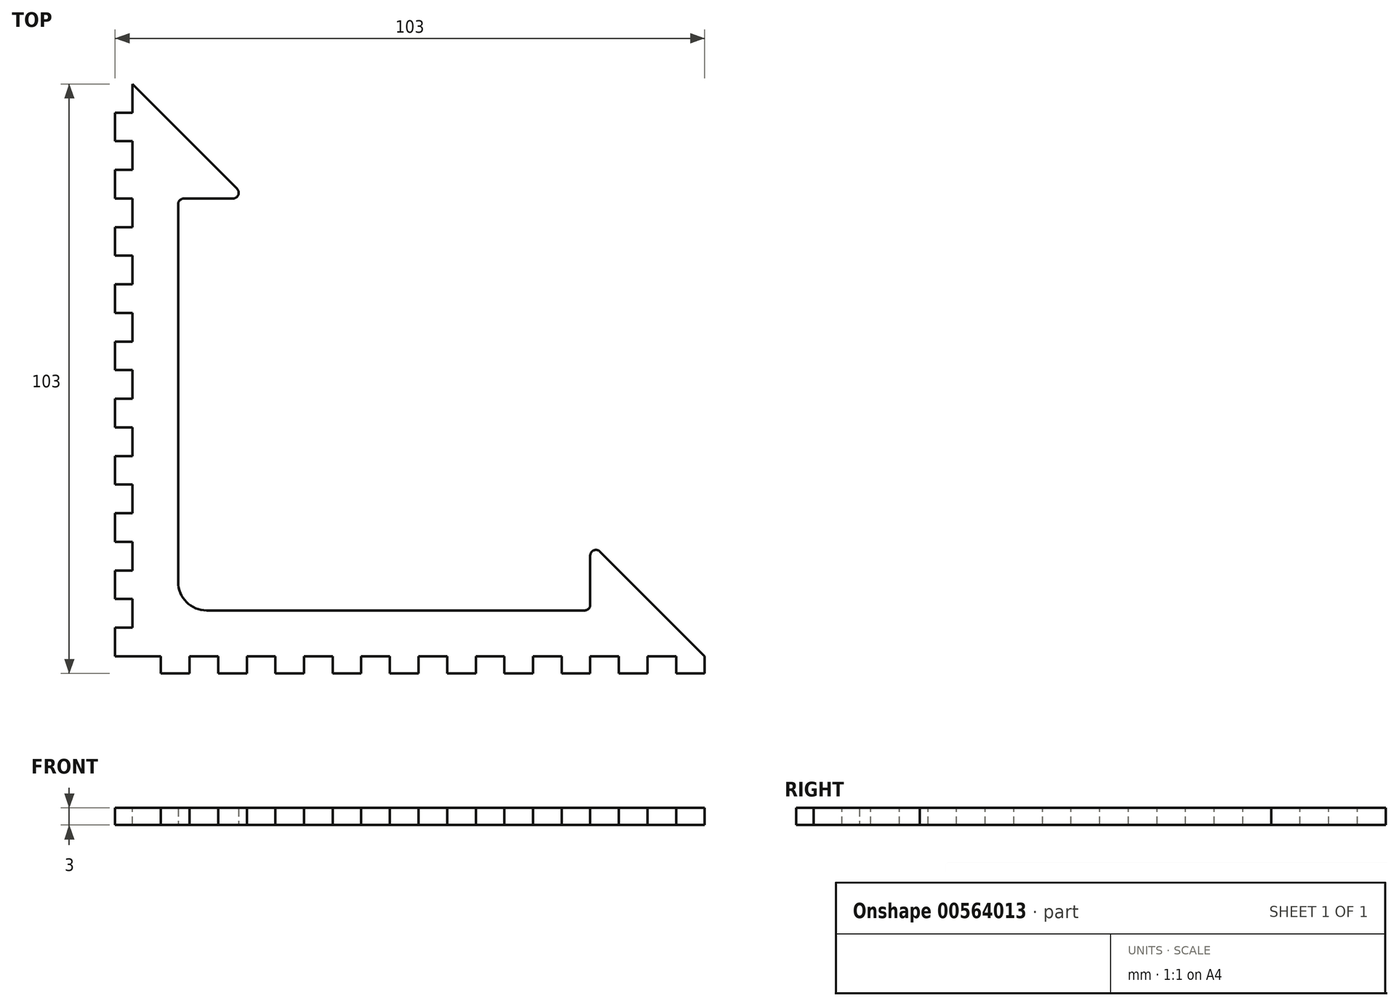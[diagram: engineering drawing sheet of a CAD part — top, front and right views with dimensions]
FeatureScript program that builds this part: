
annotation { "Feature Type Name" : "Feature", "Feature Type Description" : "" }
export const myFeature = defineFeature(function(context is Context, id is Id, definition is map)
    precondition{}
    {
        {
            var Q0;
            Q0=qCreatedBy(makeId("Top.planeOp"),FACE);
            var sketch = newSketch(context, id + "F0", { "sketchPlane" : qUnion([Q0])});
            skLineSegment(sketch, "E0", {"start": v(0, 100) * mm, "end": v(0, 0) * mm});
            skLineSegment(sketch, "E1", {"start": v(0, 0) * mm, "end": v(100, 0) * mm});
            skLineSegment(sketch, "E2", {"start": v(100, 0) * mm, "end": v(80, 20) * mm});
            skLineSegment(sketch, "E3", {"start": v(80, 20) * mm, "end": v(80, 8) * mm});
            skLineSegment(sketch, "E4", {"start": v(80, 8) * mm, "end": v(8, 8) * mm});
            skLineSegment(sketch, "E5", {"start": v(8, 8) * mm, "end": v(8, 80) * mm});
            skLineSegment(sketch, "E6", {"start": v(8, 80) * mm, "end": v(20, 80) * mm});
            skLineSegment(sketch, "E7", {"start": v(20, 80) * mm, "end": v(0, 100) * mm});
            skSolve(sketch);
        }
        {
            var Q0;
            Q0=makeQuery(id+"F0.imprint","IMPRINT",FACE,{"disambiguationData":[TD([[makeQuery(id+"F0.imprint","IMPRINT",EDGE,{"derivedFrom":sQuery(id+"F0.wireOp",EDGE,"E0")}),1.0]])]});
            extrude(context, id + "F1", {"entities" : qUnion([Q0]), "depth" : 3 * mm, "offsetDistance" : 25 * mm});
        }
        {
            var Q0;
            Q0=makeQuery(id+"F1.opExtrude","CAP_FACE",FACE,{"disambiguationData":[OSD([sQuery(id+"F0.wireOp",EDGE,"E0"),sQuery(id+"F0.wireOp",EDGE,"E1"),sQuery(id+"F0.wireOp",EDGE,"E2"),sQuery(id+"F0.wireOp",EDGE,"E3"),sQuery(id+"F0.wireOp",EDGE,"E4"),sQuery(id+"F0.wireOp",EDGE,"E5"),sQuery(id+"F0.wireOp",EDGE,"E6"),sQuery(id+"F0.wireOp",EDGE,"E7")])],"isStart":false});
            var sketch = newSketch(context, id + "F2", { "sketchPlane" : qUnion([Q0])});
            skLineSegment(sketch, "E8.bottom", {"start": v(5, 0) * mm, "end": v(10, 0) * mm});
            skLineSegment(sketch, "E8.top", {"start": v(5, -3) * mm, "end": v(10, -3) * mm});
            skLineSegment(sketch, "E8.left", {"start": v(5, 0) * mm, "end": v(5, -3) * mm});
            skLineSegment(sketch, "E8.right", {"start": v(10, 0) * mm, "end": v(10, -3) * mm});
            skLineSegment(sketch, "E9.1.0.0", {"start": v(15, 0) * mm, "end": v(20, 0) * mm});
            skLineSegment(sketch, "E9.1.0.1", {"start": v(15, 0) * mm, "end": v(15, -3) * mm});
            skLineSegment(sketch, "E9.1.0.2", {"start": v(15, -3) * mm, "end": v(20, -3) * mm});
            skLineSegment(sketch, "E9.1.0.3", {"start": v(20, 0) * mm, "end": v(20, -3) * mm});
            skLineSegment(sketch, "E9.2.0.0", {"start": v(25, 0) * mm, "end": v(30, 0) * mm});
            skLineSegment(sketch, "E9.2.0.1", {"start": v(25, 0) * mm, "end": v(25, -3) * mm});
            skLineSegment(sketch, "E9.2.0.2", {"start": v(25, -3) * mm, "end": v(30, -3) * mm});
            skLineSegment(sketch, "E9.2.0.3", {"start": v(30, 0) * mm, "end": v(30, -3) * mm});
            skLineSegment(sketch, "E9.3.0.0", {"start": v(35, 0) * mm, "end": v(40, 0) * mm});
            skLineSegment(sketch, "E9.3.0.1", {"start": v(35, 0) * mm, "end": v(35, -3) * mm});
            skLineSegment(sketch, "E9.3.0.2", {"start": v(35, -3) * mm, "end": v(40, -3) * mm});
            skLineSegment(sketch, "E9.3.0.3", {"start": v(40, 0) * mm, "end": v(40, -3) * mm});
            skLineSegment(sketch, "E9.4.0.0", {"start": v(45, 0) * mm, "end": v(50, 0) * mm});
            skLineSegment(sketch, "E9.4.0.1", {"start": v(45, 0) * mm, "end": v(45, -3) * mm});
            skLineSegment(sketch, "E9.4.0.2", {"start": v(45, -3) * mm, "end": v(50, -3) * mm});
            skLineSegment(sketch, "E9.4.0.3", {"start": v(50, 0) * mm, "end": v(50, -3) * mm});
            skLineSegment(sketch, "E9.direction1", {"start": v(5, 0) * mm, "end": v(15, 0) * mm, "construction": true});
            skLineSegment(sketch, "E10.0.5.0", {"start": v(55, 0) * mm, "end": v(60, 0) * mm});
            skLineSegment(sketch, "E10.3.5.0", {"start": v(55, 0) * mm, "end": v(55, -3) * mm});
            skLineSegment(sketch, "E10.6.5.0", {"start": v(55, -3) * mm, "end": v(60, -3) * mm});
            skLineSegment(sketch, "E10.9.5.0", {"start": v(60, 0) * mm, "end": v(60, -3) * mm});
            skLineSegment(sketch, "E10.0.6.0", {"start": v(65, 0) * mm, "end": v(70, 0) * mm});
            skLineSegment(sketch, "E10.3.6.0", {"start": v(65, 0) * mm, "end": v(65, -3) * mm});
            skLineSegment(sketch, "E10.6.6.0", {"start": v(65, -3) * mm, "end": v(70, -3) * mm});
            skLineSegment(sketch, "E10.9.6.0", {"start": v(70, 0) * mm, "end": v(70, -3) * mm});
            skLineSegment(sketch, "E10.0.7.0", {"start": v(75, 0) * mm, "end": v(80, 0) * mm});
            skLineSegment(sketch, "E10.3.7.0", {"start": v(75, 0) * mm, "end": v(75, -3) * mm});
            skLineSegment(sketch, "E10.6.7.0", {"start": v(75, -3) * mm, "end": v(80, -3) * mm});
            skLineSegment(sketch, "E10.9.7.0", {"start": v(80, 0) * mm, "end": v(80, -3) * mm});
            skLineSegment(sketch, "E10.0.8.0", {"start": v(85, 0) * mm, "end": v(90, 0) * mm});
            skLineSegment(sketch, "E10.3.8.0", {"start": v(85, 0) * mm, "end": v(85, -3) * mm});
            skLineSegment(sketch, "E10.6.8.0", {"start": v(85, -3) * mm, "end": v(90, -3) * mm});
            skLineSegment(sketch, "E10.9.8.0", {"start": v(90, 0) * mm, "end": v(90, -3) * mm});
            skLineSegment(sketch, "E10.0.9.0", {"start": v(95, 0) * mm, "end": v(100, 0) * mm});
            skLineSegment(sketch, "E10.3.9.0", {"start": v(95, 0) * mm, "end": v(95, -3) * mm});
            skLineSegment(sketch, "E10.6.9.0", {"start": v(95, -3) * mm, "end": v(100, -3) * mm});
            skLineSegment(sketch, "E10.9.9.0", {"start": v(100, 0) * mm, "end": v(100, -3) * mm});
            skSolve(sketch);
        }
        {
            var Q0;
            {var subQ2=sQuery(id+"F2.wireOp",EDGE,"E8.bottom");Q0=makeQuery(id+"F2.imprint","IMPRINT",FACE,{"disambiguationData":[TD([[makeQuery(id+"F2.imprint","IMPRINT",EDGE,{"derivedFrom":subQ2}),1.0]])]});}
            var sketch = newSketch(context, id + "F3", { "sketchPlane" : qUnion([Q0])});
            skLineSegment(sketch, "E11.bottom", {"start": v(0, 0) * mm, "end": v(-3, 0) * mm});
            skLineSegment(sketch, "E11.top", {"start": v(0, 5) * mm, "end": v(-3, 5) * mm});
            skLineSegment(sketch, "E11.left", {"start": v(0, 0) * mm, "end": v(0, 5) * mm});
            skLineSegment(sketch, "E11.right", {"start": v(-3, 0) * mm, "end": v(-3, 5) * mm});
            skLineSegment(sketch, "E12.0.1.0", {"start": v(0, 15) * mm, "end": v(-3, 15) * mm});
            skLineSegment(sketch, "E12.0.1.1", {"start": v(-3, 10) * mm, "end": v(-3, 15) * mm});
            skLineSegment(sketch, "E12.0.1.2", {"start": v(0, 10) * mm, "end": v(0, 15) * mm});
            skLineSegment(sketch, "E12.0.1.3", {"start": v(0, 10) * mm, "end": v(-3, 10) * mm});
            skLineSegment(sketch, "E12.0.2.0", {"start": v(0, 25) * mm, "end": v(-3, 25) * mm});
            skLineSegment(sketch, "E12.0.2.1", {"start": v(-3, 20) * mm, "end": v(-3, 25) * mm});
            skLineSegment(sketch, "E12.0.2.2", {"start": v(0, 20) * mm, "end": v(0, 25) * mm});
            skLineSegment(sketch, "E12.0.2.3", {"start": v(0, 20) * mm, "end": v(-3, 20) * mm});
            skLineSegment(sketch, "E12.0.3.0", {"start": v(0, 35) * mm, "end": v(-3, 35) * mm});
            skLineSegment(sketch, "E12.0.3.1", {"start": v(-3, 30) * mm, "end": v(-3, 35) * mm});
            skLineSegment(sketch, "E12.0.3.2", {"start": v(0, 30) * mm, "end": v(0, 35) * mm});
            skLineSegment(sketch, "E12.0.3.3", {"start": v(0, 30) * mm, "end": v(-3, 30) * mm});
            skLineSegment(sketch, "E12.0.4.0", {"start": v(0, 45) * mm, "end": v(-3, 45) * mm});
            skLineSegment(sketch, "E12.0.4.1", {"start": v(-3, 40) * mm, "end": v(-3, 45) * mm});
            skLineSegment(sketch, "E12.0.4.2", {"start": v(0, 40) * mm, "end": v(0, 45) * mm});
            skLineSegment(sketch, "E12.0.4.3", {"start": v(0, 40) * mm, "end": v(-3, 40) * mm});
            skLineSegment(sketch, "E12.direction1", {"start": v(-3, 5) * mm, "end": v(13.8, 5) * mm, "construction": true});
            skLineSegment(sketch, "E12.direction2", {"start": v(-3, 5) * mm, "end": v(-3, 15) * mm, "construction": true});
            skLineSegment(sketch, "E13.0.0.5", {"start": v(0, 55) * mm, "end": v(-3, 55) * mm});
            skLineSegment(sketch, "E13.3.0.5", {"start": v(-3, 50) * mm, "end": v(-3, 55) * mm});
            skLineSegment(sketch, "E13.6.0.5", {"start": v(0, 50) * mm, "end": v(0, 55) * mm});
            skLineSegment(sketch, "E13.9.0.5", {"start": v(0, 50) * mm, "end": v(-3, 50) * mm});
            skLineSegment(sketch, "E13.0.0.6", {"start": v(0, 65) * mm, "end": v(-3, 65) * mm});
            skLineSegment(sketch, "E13.3.0.6", {"start": v(-3, 60) * mm, "end": v(-3, 65) * mm});
            skLineSegment(sketch, "E13.6.0.6", {"start": v(0, 60) * mm, "end": v(0, 65) * mm});
            skLineSegment(sketch, "E13.9.0.6", {"start": v(0, 60) * mm, "end": v(-3, 60) * mm});
            skLineSegment(sketch, "E13.0.0.7", {"start": v(0, 75) * mm, "end": v(-3, 75) * mm});
            skLineSegment(sketch, "E13.3.0.7", {"start": v(-3, 70) * mm, "end": v(-3, 75) * mm});
            skLineSegment(sketch, "E13.6.0.7", {"start": v(0, 70) * mm, "end": v(0, 75) * mm});
            skLineSegment(sketch, "E13.9.0.7", {"start": v(0, 70) * mm, "end": v(-3, 70) * mm});
            skLineSegment(sketch, "E13.0.0.8", {"start": v(0, 85) * mm, "end": v(-3, 85) * mm});
            skLineSegment(sketch, "E13.3.0.8", {"start": v(-3, 80) * mm, "end": v(-3, 85) * mm});
            skLineSegment(sketch, "E13.6.0.8", {"start": v(0, 80) * mm, "end": v(0, 85) * mm});
            skLineSegment(sketch, "E13.9.0.8", {"start": v(0, 80) * mm, "end": v(-3, 80) * mm});
            skLineSegment(sketch, "E13.0.0.9", {"start": v(0, 95) * mm, "end": v(-3, 95) * mm});
            skLineSegment(sketch, "E13.3.0.9", {"start": v(-3, 90) * mm, "end": v(-3, 95) * mm});
            skLineSegment(sketch, "E13.6.0.9", {"start": v(0, 90) * mm, "end": v(0, 95) * mm});
            skLineSegment(sketch, "E13.9.0.9", {"start": v(0, 90) * mm, "end": v(-3, 90) * mm});
            skSolve(sketch);
        }
        {
            var Q0;
            Q0=makeQuery(id+"F3.imprint","IMPRINT",FACE,{"disambiguationData":[TD([[makeQuery(id+"F3.imprint","IMPRINT",EDGE,{"derivedFrom":sQuery(id+"F3.wireOp",EDGE,"E12.0.4.0")}),1.0]])]});
            var Q1;
            Q1=makeQuery(id+"F3.imprint","IMPRINT",FACE,{"disambiguationData":[TD([[makeQuery(id+"F3.imprint","IMPRINT",EDGE,{"derivedFrom":sQuery(id+"F3.wireOp",EDGE,"E12.0.3.0")}),1.0]])]});
            var Q2;
            Q2=makeQuery(id+"F3.imprint","IMPRINT",FACE,{"disambiguationData":[TD([[makeQuery(id+"F3.imprint","IMPRINT",EDGE,{"derivedFrom":sQuery(id+"F3.wireOp",EDGE,"E12.0.2.0")}),1.0]])]});
            var Q3;
            Q3=makeQuery(id+"F3.imprint","IMPRINT",FACE,{"disambiguationData":[TD([[makeQuery(id+"F3.imprint","IMPRINT",EDGE,{"derivedFrom":sQuery(id+"F3.wireOp",EDGE,"E12.0.1.0")}),1.0]])]});
            var Q4;
            Q4=makeQuery(id+"F3.imprint","IMPRINT",FACE,{"disambiguationData":[TD([[makeQuery(id+"F3.imprint","IMPRINT",EDGE,{"derivedFrom":sQuery(id+"F3.wireOp",EDGE,"E11.bottom")}),-1.0]])]});
            var Q5;
            Q5=makeQuery(id+"F2.imprint","IMPRINT",FACE,{"disambiguationData":[TD([[makeQuery(id+"F2.imprint","IMPRINT",EDGE,{"derivedFrom":sQuery(id+"F2.wireOp",EDGE,"E8.bottom")}),-1.0]])]});
            var Q6;
            Q6=makeQuery(id+"F2.imprint","IMPRINT",FACE,{"disambiguationData":[TD([[makeQuery(id+"F2.imprint","IMPRINT",EDGE,{"derivedFrom":sQuery(id+"F2.wireOp",EDGE,"E9.1.0.0")}),-1.0]])]});
            var Q7;
            Q7=makeQuery(id+"F2.imprint","IMPRINT",FACE,{"disambiguationData":[TD([[makeQuery(id+"F2.imprint","IMPRINT",EDGE,{"derivedFrom":sQuery(id+"F2.wireOp",EDGE,"E9.2.0.0")}),-1.0]])]});
            var Q8;
            Q8=makeQuery(id+"F2.imprint","IMPRINT",FACE,{"disambiguationData":[TD([[makeQuery(id+"F2.imprint","IMPRINT",EDGE,{"derivedFrom":sQuery(id+"F2.wireOp",EDGE,"E9.3.0.0")}),-1.0]])]});
            var Q9;
            Q9=makeQuery(id+"F2.imprint","IMPRINT",FACE,{"disambiguationData":[TD([[makeQuery(id+"F2.imprint","IMPRINT",EDGE,{"derivedFrom":sQuery(id+"F2.wireOp",EDGE,"E9.4.0.0")}),-1.0]])]});
            var Q10;
            Q10=makeQuery(id+"F3.imprint","IMPRINT",FACE,{"disambiguationData":[TD([[makeQuery(id+"F3.imprint","IMPRINT",EDGE,{"derivedFrom":sQuery(id+"F3.wireOp",EDGE,"E13.0.0.5")}),1.0]])]});
            var Q11;
            {var subQ13=sQuery(id+"F3.wireOp",EDGE,"E11.left");Q11=makeQuery(id+"F3.imprint","IMPRINT",FACE,{"disambiguationData":[TD([[makeQuery(id+"F3.imprint","IMPRINT",EDGE,{"derivedFrom":subQ13}),1.0]])]});}
            var Q12;
            Q12=makeQuery(id+"F3.imprint","IMPRINT",FACE,{"disambiguationData":[TD([[makeQuery(id+"F3.imprint","IMPRINT",EDGE,{"derivedFrom":sQuery(id+"F3.wireOp",EDGE,"E13.0.0.7")}),1.0]])]});
            var Q13;
            Q13=makeQuery(id+"F3.imprint","IMPRINT",FACE,{"disambiguationData":[TD([[makeQuery(id+"F3.imprint","IMPRINT",EDGE,{"derivedFrom":sQuery(id+"F3.wireOp",EDGE,"E13.0.0.8")}),1.0]])]});
            var Q14;
            Q14=makeQuery(id+"F3.imprint","IMPRINT",FACE,{"disambiguationData":[TD([[makeQuery(id+"F3.imprint","IMPRINT",EDGE,{"derivedFrom":sQuery(id+"F3.wireOp",EDGE,"E13.0.0.9")}),1.0]])]});
            var Q15;
            Q15=makeQuery(id+"F3.imprint","IMPRINT",FACE,{"disambiguationData":[TD([[makeQuery(id+"F3.imprint","IMPRINT",EDGE,{"derivedFrom":sQuery(id+"F3.wireOp",EDGE,"E13.0.0.6")}),1.0]])]});
            var Q16;
            Q16=makeQuery(id+"F2.imprint","IMPRINT",FACE,{"disambiguationData":[TD([[makeQuery(id+"F2.imprint","IMPRINT",EDGE,{"derivedFrom":sQuery(id+"F2.wireOp",EDGE,"E10.0.5.0")}),-1.0]])]});
            var Q17;
            Q17=makeQuery(id+"F2.imprint","IMPRINT",FACE,{"disambiguationData":[TD([[makeQuery(id+"F2.imprint","IMPRINT",EDGE,{"derivedFrom":sQuery(id+"F2.wireOp",EDGE,"E10.0.6.0")}),-1.0]])]});
            var Q18;
            Q18=makeQuery(id+"F2.imprint","IMPRINT",FACE,{"disambiguationData":[TD([[makeQuery(id+"F2.imprint","IMPRINT",EDGE,{"derivedFrom":sQuery(id+"F2.wireOp",EDGE,"E10.0.7.0")}),-1.0]])]});
            var Q19;
            Q19=makeQuery(id+"F2.imprint","IMPRINT",FACE,{"disambiguationData":[TD([[makeQuery(id+"F2.imprint","IMPRINT",EDGE,{"derivedFrom":sQuery(id+"F2.wireOp",EDGE,"E10.0.8.0")}),-1.0]])]});
            var Q20;
            Q20=makeQuery(id+"F2.imprint","IMPRINT",FACE,{"disambiguationData":[TD([[makeQuery(id+"F2.imprint","IMPRINT",EDGE,{"derivedFrom":sQuery(id+"F2.wireOp",EDGE,"E10.0.9.0")}),-1.0]])]});
            extrude(context, id + "F4", {"entities" : qUnion([Q0, Q1, Q2, Q3, Q4, Q5, Q6, Q7, Q8, Q9, Q10, Q11, Q12, Q13, Q14, Q15, Q16, Q17, Q18, Q19, Q20]), "operationType" : NewBodyOperationType.ADD, "oppositeDirection" : true, "depth" : 3 * mm, "offsetDistance" : 25 * mm});
        }
        {
            var Q0;
            Q0=makeQuery(id+"F1.opExtrude","SWEPT_EDGE",EDGE,{"disambiguationData":[OSD([sQuery(id+"F0.wireOp",EDGE,"E2"),sQuery(id+"F0.wireOp",EDGE,"E3")])]});
            var Q1;
            Q1=makeQuery(id+"F1.opExtrude","SWEPT_EDGE",EDGE,{"disambiguationData":[OSD([sQuery(id+"F0.wireOp",EDGE,"E5"),sQuery(id+"F0.wireOp",EDGE,"E6")])]});
            var Q2;
            Q2=makeQuery(id+"F1.opExtrude","SWEPT_EDGE",EDGE,{"disambiguationData":[OSD([sQuery(id+"F0.wireOp",EDGE,"E6"),sQuery(id+"F0.wireOp",EDGE,"E7")])]});
            var Q3;
            Q3=makeQuery(id+"F1.opExtrude","SWEPT_EDGE",EDGE,{"disambiguationData":[OSD([sQuery(id+"F0.wireOp",EDGE,"E3"),sQuery(id+"F0.wireOp",EDGE,"E4")])]});
            fillet(context, id + "F5", {"entities" : qUnion([Q0, Q1, Q2, Q3]), "radius" : 1 * mm, "tangentPropagation" : true, "allowEdgeOverflow" : false});
        }
        {
            var Q0;
            Q0=makeQuery(id+"F1.opExtrude","SWEPT_EDGE",EDGE,{"disambiguationData":[OSD([sQuery(id+"F0.wireOp",EDGE,"E4"),sQuery(id+"F0.wireOp",EDGE,"E5")])]});
            fillet(context, id + "F6", {"entities" : qUnion([Q0]), "radius" : 5 * mm, "tangentPropagation" : true, "allowEdgeOverflow" : false});
        }
    });
